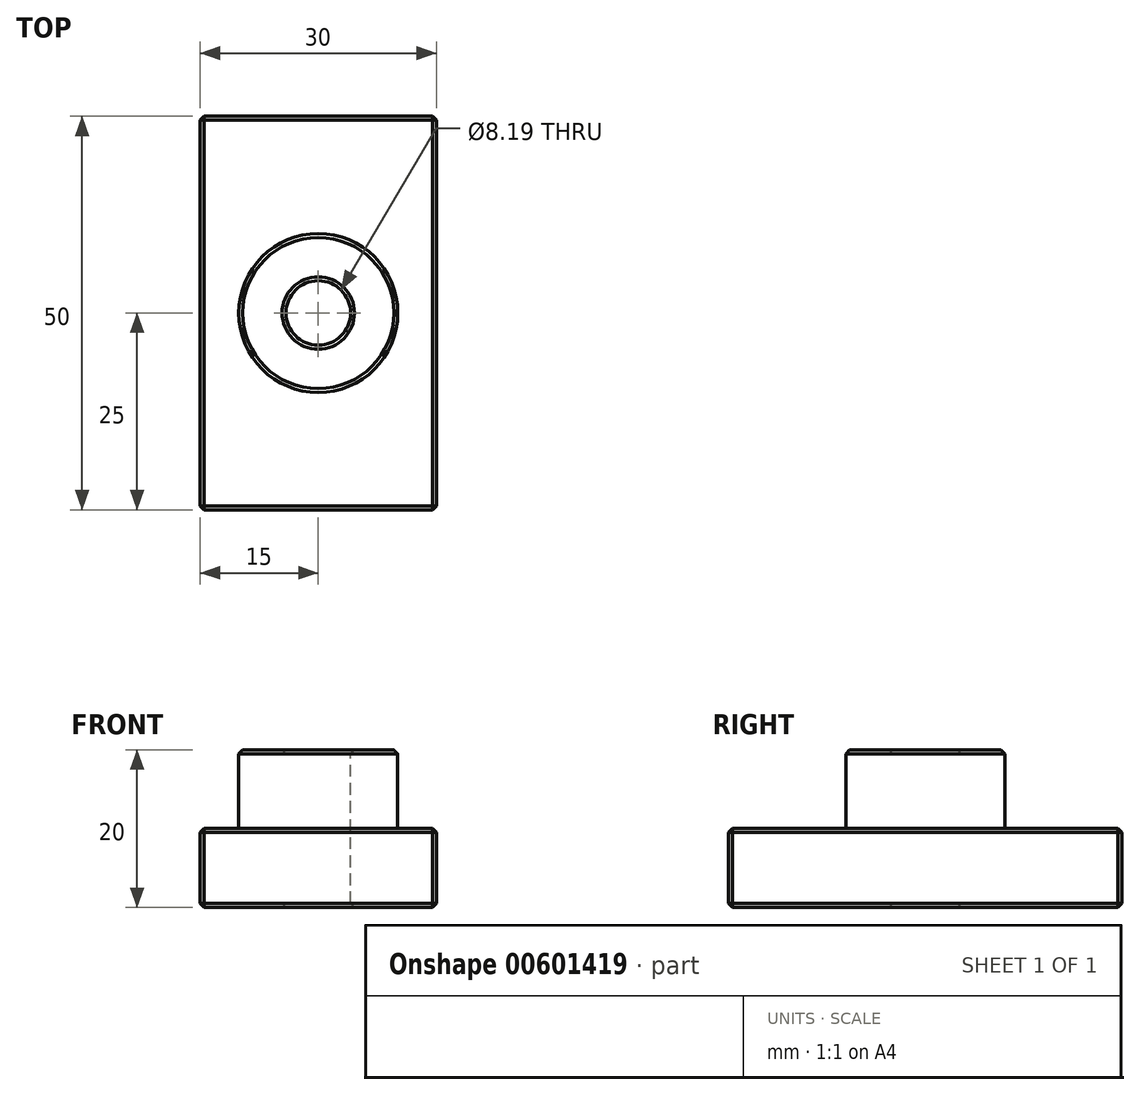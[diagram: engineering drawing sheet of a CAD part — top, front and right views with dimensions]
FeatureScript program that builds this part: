
annotation { "Feature Type Name" : "Feature", "Feature Type Description" : "" }
export const myFeature = defineFeature(function(context is Context, id is Id, definition is map)
    precondition{}
    {
        {
            var Q0;
            Q0=qCreatedBy(makeId("Top.planeOp"),FACE);
            var sketch = newSketch(context, id + "F0", { "sketchPlane" : qUnion([Q0])});
            skLineSegment(sketch, "E0.bottom", {"start": v(-15, 25) * mm, "end": v(15, 25) * mm});
            skLineSegment(sketch, "E0.top", {"start": v(-15, -25) * mm, "end": v(15, -25) * mm});
            skLineSegment(sketch, "E0.left", {"start": v(-15, 25) * mm, "end": v(-15, -25) * mm});
            skLineSegment(sketch, "E0.right", {"start": v(15, 25) * mm, "end": v(15, -25) * mm});
            skPoint(sketch, "E0.middle", {"position": v(0, 0) * mm});
            skSolve(sketch);
        }
        {
            var Q0;
            Q0=makeQuery(id+"F0.imprint","IMPRINT",FACE,{"disambiguationData":[TD([[makeQuery(id+"F0.imprint","IMPRINT",EDGE,{"derivedFrom":sQuery(id+"F0.wireOp",EDGE,"j5xDlvvR-ICA3-1iFV-k2qC-1I0Etjp5m1a9")}),-1.0]])]});
            var Q1;
            Q1=makeQuery(id+"F0.imprint","IMPRINT",FACE,{"disambiguationData":[TD([[makeQuery(id+"F0.imprint","IMPRINT",EDGE,{"derivedFrom":sQuery(id+"F0.wireOp",EDGE,"E0.bottom")}),-1.0]])]});
            extrude(context, id + "F1", {"entities" : qUnion([Q0, Q1]), "oppositeDirection" : true, "depth" : 10 * mm, "offsetDistance" : 25 * mm});
        }
        {
            var Q0;
            Q0=qCreatedBy(makeId("Top.planeOp"),FACE);
            var sketch = newSketch(context, id + "F2", { "sketchPlane" : qUnion([Q0])});
            skCircle(sketch, "E1", {"center": v(0, 0) * mm, "radius": 10.1 * mm});
            skSolve(sketch);
        }
        {
            var Q0;
            Q0 = qSketchRegion(id + "F2", true);
            extrude(context, id + "F3", {"entities" : qUnion([Q0]), "operationType" : NewBodyOperationType.ADD, "depth" : 10 * mm, "offsetDistance" : 25 * mm});
        }
        {
            var Q0;
            Q0=qCreatedBy(makeId("Top.planeOp"),FACE);
            var sketch = newSketch(context, id + "F4", { "sketchPlane" : qUnion([Q0])});
            skCircle(sketch, "E2", {"center": v(0, 0) * mm, "radius": 4.1 * mm});
            skSolve(sketch);
        }
        {
            var Q0;
            Q0 = qSketchRegion(id + "F4", true);
            extrude(context, id + "F5", {"entities" : qUnion([Q0]), "operationType" : NewBodyOperationType.REMOVE, "oppositeDirection" : true, "depth" : 25 * mm, "offsetDistance" : 25 * mm, "hasSecondDirection" : true, "secondDirectionOppositeDirection" : false, "secondDirectionDepth" : 25 * mm});
        }
        {
            var Q0;
            Q0=makeQuery(id+"F1.opExtrude","CAP_EDGE",EDGE,{"disambiguationData":[OSD([sQuery(id+"F0.wireOp",EDGE,"E0.right")])],"isStart":true});
            var Q1;
            Q1=makeQuery(id+"F1.opExtrude","CAP_EDGE",EDGE,{"disambiguationData":[OSD([sQuery(id+"F0.wireOp",EDGE,"E0.top")])],"isStart":true});
            var Q2;
            Q2=makeQuery(id+"F1.opExtrude","CAP_EDGE",EDGE,{"disambiguationData":[OSD([sQuery(id+"F0.wireOp",EDGE,"E0.left")])],"isStart":true});
            var Q3;
            Q3=makeQuery(id+"F1.opExtrude","CAP_EDGE",EDGE,{"disambiguationData":[OSD([sQuery(id+"F0.wireOp",EDGE,"E0.bottom")])],"isStart":true});
            var Q4;
            Q4=makeQuery(id+"F3.opExtrude","CAP_EDGE",EDGE,{"disambiguationData":[OSD([sQuery(id+"F2.wireOp",EDGE,"E1")])],"isStart":false});
            var Q5;
            Q5=makeQuery(id+"F5.boolean.opBoolean","INTERSECT",EDGE,{"derivedFrom":[makeQuery(id+"F3.opExtrude","CAP_FACE",FACE,{"disambiguationData":[OSD([sQuery(id+"F2.wireOp",EDGE,"E1")])],"isStart":false}),makeQuery(id+"F5.opExtrude","SWEPT_FACE",FACE,{"disambiguationData":[OSD([sQuery(id+"F4.wireOp",EDGE,"E2")])]})]});
            var Q6;
            Q6=makeQuery(id+"F1.opExtrude","SWEPT_EDGE",EDGE,{"disambiguationData":[OSD([sQuery(id+"F0.wireOp",EDGE,"E0.top"),sQuery(id+"F0.wireOp",EDGE,"E0.right")])]});
            var Q7;
            Q7=makeQuery(id+"F1.opExtrude","SWEPT_EDGE",EDGE,{"disambiguationData":[OSD([sQuery(id+"F0.wireOp",EDGE,"E0.bottom"),sQuery(id+"F0.wireOp",EDGE,"E0.right")])]});
            var Q8;
            Q8=makeQuery(id+"F1.opExtrude","SWEPT_EDGE",EDGE,{"disambiguationData":[OSD([sQuery(id+"F0.wireOp",EDGE,"E0.top"),sQuery(id+"F0.wireOp",EDGE,"E0.left")])]});
            var Q9;
            Q9=makeQuery(id+"F1.opExtrude","CAP_EDGE",EDGE,{"disambiguationData":[OSD([sQuery(id+"F0.wireOp",EDGE,"E0.top")])],"isStart":false});
            var Q10;
            Q10=makeQuery(id+"F1.opExtrude","CAP_EDGE",EDGE,{"disambiguationData":[OSD([sQuery(id+"F0.wireOp",EDGE,"E0.right")])],"isStart":false});
            var Q11;
            Q11=makeQuery(id+"F1.opExtrude","SWEPT_EDGE",EDGE,{"disambiguationData":[OSD([sQuery(id+"F0.wireOp",EDGE,"E0.bottom"),sQuery(id+"F0.wireOp",EDGE,"E0.left")])]});
            var Q12;
            Q12=makeQuery(id+"F1.opExtrude","CAP_EDGE",EDGE,{"disambiguationData":[OSD([sQuery(id+"F0.wireOp",EDGE,"E0.left")])],"isStart":false});
            var Q13;
            Q13=makeQuery(id+"F1.opExtrude","CAP_EDGE",EDGE,{"disambiguationData":[OSD([sQuery(id+"F0.wireOp",EDGE,"E0.bottom")])],"isStart":false});
            chamfer(context, id + "F6", {"entities" : qUnion([Q0, Q1, Q2, Q3, Q4, Q5, Q6, Q7, Q8, Q9, Q10, Q11, Q12, Q13]), "width" : 0.5 * mm, "tangentPropagation" : true});
        }
        {
            var Q0;
            Q0=makeQuery(id+"F5.boolean.opBoolean","INTERSECT",EDGE,{"derivedFrom":[makeQuery(id+"F1.opExtrude","CAP_FACE",FACE,{"disambiguationData":[OSD([sQuery(id+"F0.wireOp",EDGE,"E0.bottom"),sQuery(id+"F0.wireOp",EDGE,"E0.top"),sQuery(id+"F0.wireOp",EDGE,"E0.left"),sQuery(id+"F0.wireOp",EDGE,"E0.right")])],"isStart":false}),makeQuery(id+"F5.opExtrude","SWEPT_FACE",FACE,{"disambiguationData":[OSD([sQuery(id+"F4.wireOp",EDGE,"E2")])]})]});
            chamfer(context, id + "F7", {"entities" : qUnion([Q0]), "width" : 0.5 * mm, "tangentPropagation" : true});
        }
    });
